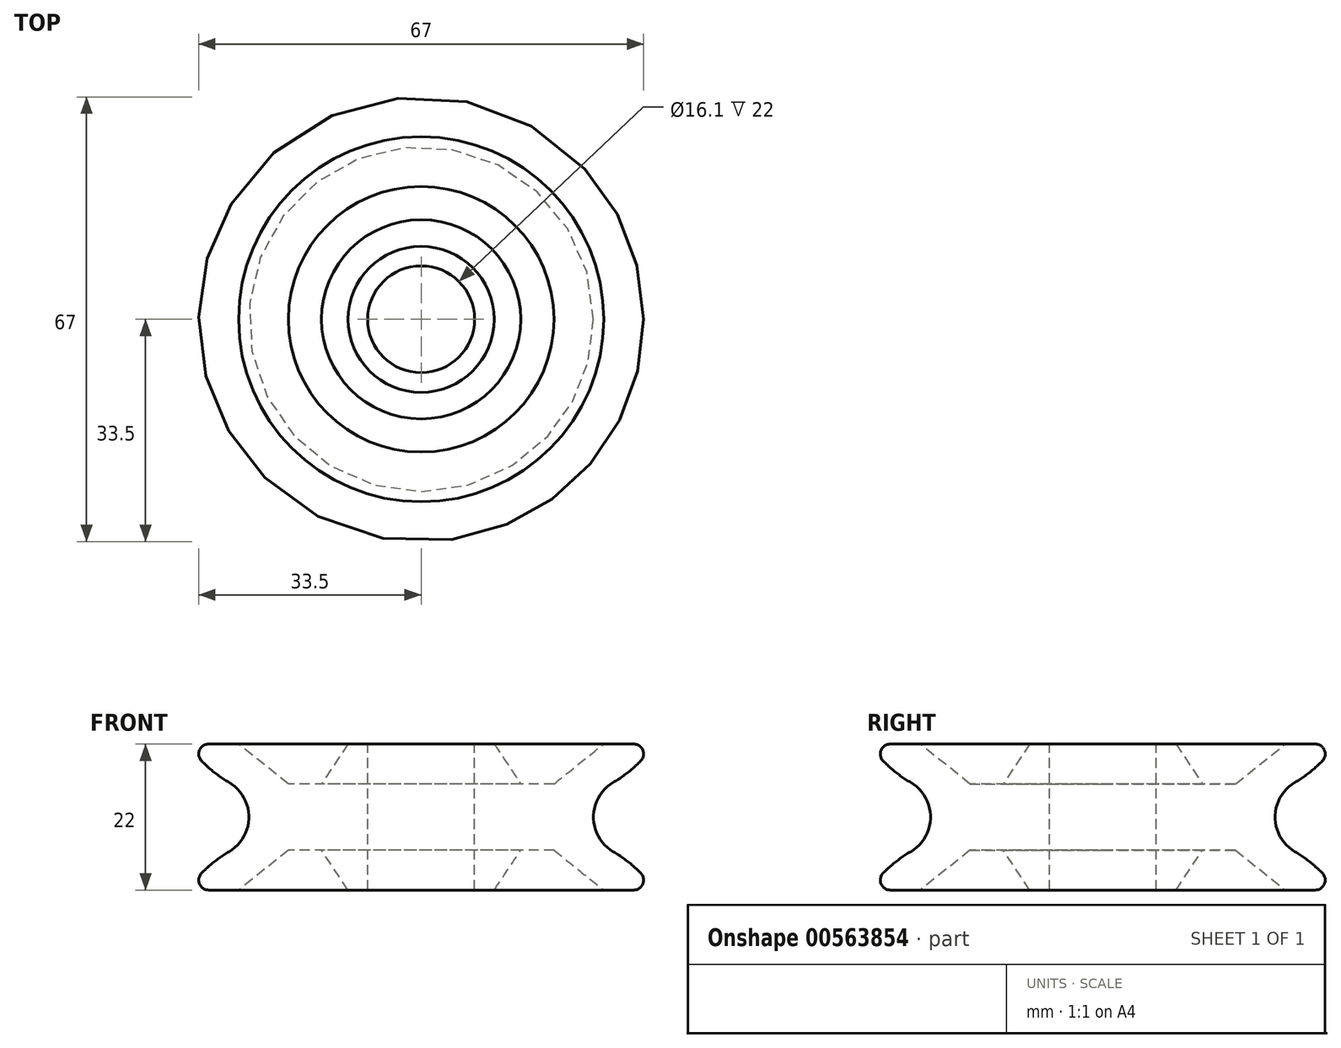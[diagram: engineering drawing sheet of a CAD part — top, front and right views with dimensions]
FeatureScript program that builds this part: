
annotation { "Feature Type Name" : "Feature", "Feature Type Description" : "" }
export const myFeature = defineFeature(function(context is Context, id is Id, definition is map)
    precondition{}
    {
        {
            var Q0;
            Q0=qCreatedBy(makeId("Front.planeOp"),FACE);
            var sketch = newSketch(context, id + "F0", { "sketchPlane" : qUnion([Q0])});
            skLineSegment(sketch, "E0", {"start": v(0, 69.19) * mm, "end": v(0, -62.03) * mm, "construction": true});
            skArc(sketch, "E1", {"start": v(33.07, 8.45) * mm, "mid": v(33.38, 10.08) * mm, "end": v(32, 11) * mm});
            skArc(sketch, "E2", {"start": v(28.93, 5.21) * mm, "mid": v(31.1, 6.7) * mm, "end": v(33.07, 8.45) * mm});
            skLineSegment(sketch, "E3", {"start": v(32, 11) * mm, "end": v(27.5, 11) * mm});
            skLineSegment(sketch, "E4", {"start": v(0, 0) * mm, "end": v(68.76, 0) * mm, "construction": true});
            skLineSegment(sketch, "E5.MirrorCS", {"start": v(32, -11) * mm, "end": v(27.5, -11) * mm});
            skArc(sketch, "E6.MirrorCS", {"start": v(33.07, -8.45) * mm, "mid": v(33.38, -10.08) * mm, "end": v(32, -11) * mm});
            skArc(sketch, "E7.MirrorCS", {"start": v(28.93, -5.21) * mm, "mid": v(31.1, -6.7) * mm, "end": v(33.07, -8.45) * mm});
            skLineSegment(sketch, "E8", {"start": v(8.05, 11) * mm, "end": v(8.05, -11) * mm});
            skPoint(sketch, "E9.orphan", {"position": v(0, 11) * mm});
            skPoint(sketch, "E10.orphan", {"position": v(0, -11) * mm});
            skArc(sketch, "E11", {"start": v(28.93, 5.21) * mm, "mid": v(25.95, 0) * mm, "end": v(28.93, -5.21) * mm});
            skLineSegment(sketch, "E12", {"start": v(11, 11) * mm, "end": v(15, 5) * mm});
            skLineSegment(sketch, "E13", {"start": v(15, 5) * mm, "end": v(20, 5) * mm});
            skLineSegment(sketch, "E14", {"start": v(20, 5) * mm, "end": v(27.5, 11) * mm});
            skLineSegment(sketch, "E15.trimOffspring", {"start": v(11, 11) * mm, "end": v(8.05, 11) * mm});
            skLineSegment(sketch, "E16.MirrorCS", {"start": v(15, -5) * mm, "end": v(20, -5) * mm});
            skLineSegment(sketch, "E17.MirrorCS", {"start": v(11, -11) * mm, "end": v(15, -5) * mm});
            skLineSegment(sketch, "E18.MirrorCS", {"start": v(20, -5) * mm, "end": v(27.5, -11) * mm});
            skLineSegment(sketch, "E19.trimOffspring", {"start": v(11, -11) * mm, "end": v(8.05, -11) * mm});
            skSolve(sketch);
        }
        {
            var Q0;
            Q0 = qSketchRegion(id + "F0", true);
            var Q1;
            Q1=sQuery(id+"F0.wireOp",EDGE,"E0");
            revolve(context, id + "F1", {"entities" : qUnion([Q0]), "axis" : qUnion([Q1]), "revolveType" : RevolveType.FULL});
        }
    });
